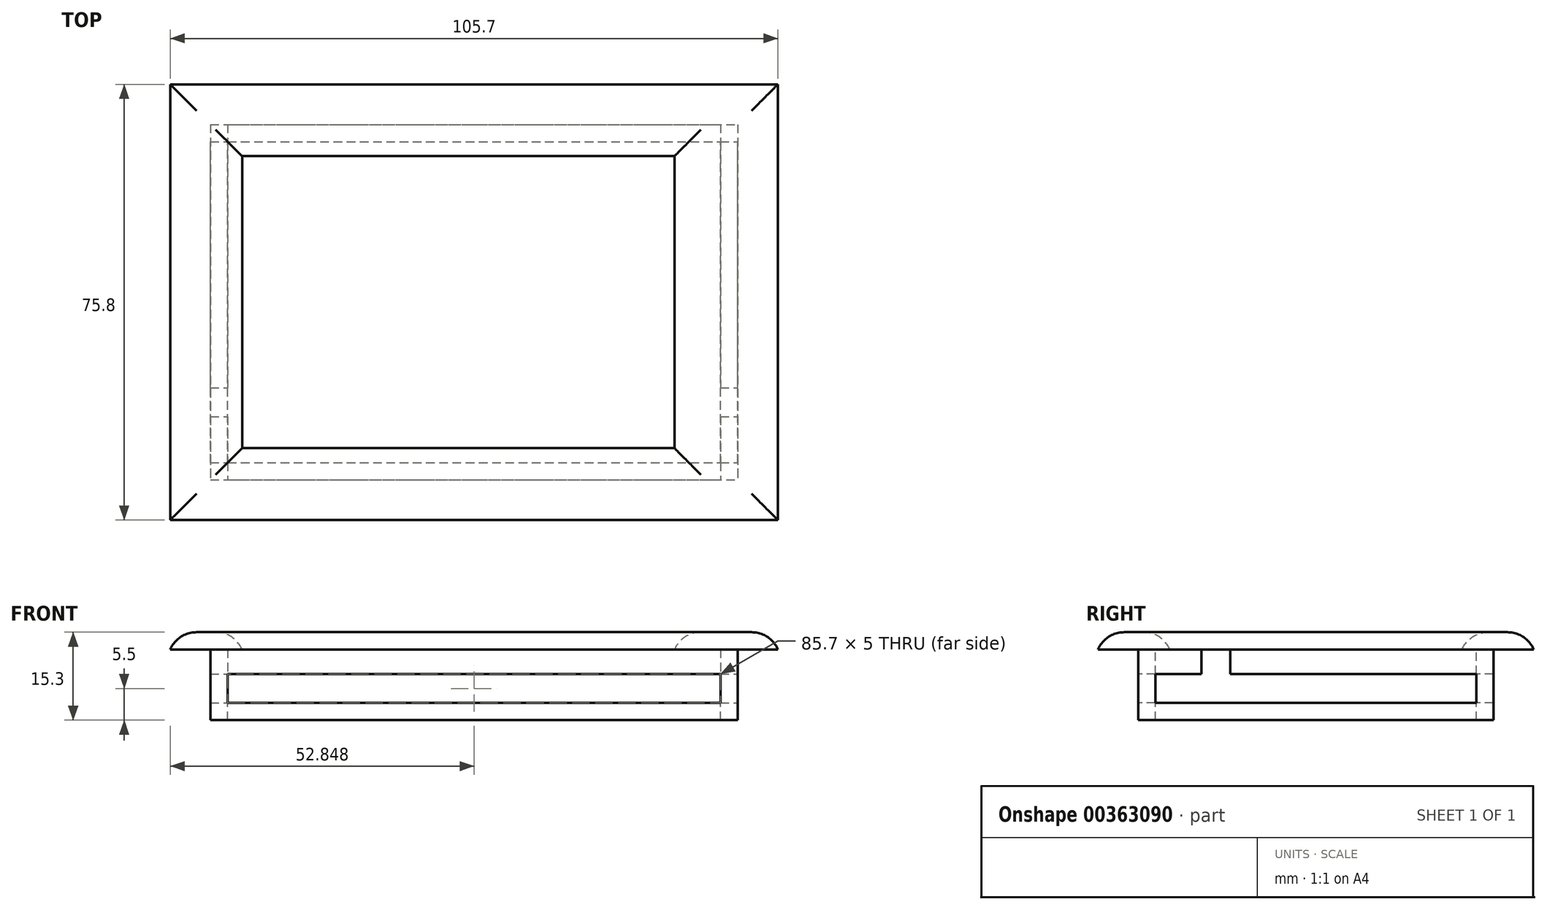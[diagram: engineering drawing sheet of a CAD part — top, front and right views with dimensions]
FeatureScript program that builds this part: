
annotation { "Feature Type Name" : "Feature", "Feature Type Description" : "" }
export const myFeature = defineFeature(function(context is Context, id is Id, definition is map)
    precondition{}
    {
        {
            assignVariable(context, id + "F0", {"name" : "tykkelse", "anyValue" : 6.3 * mm});
        }
        {
            assignVariable(context, id + "F1", {"name" : "godstykkelse", "anyValue" : 3 * mm});
        }
        {
            var Q0;
            Q0=qCreatedBy(makeId("Top.planeOp"),FACE);
            var sketch = newSketch(context, id + "F2", { "sketchPlane" : qUnion([Q0])});
            skLineSegment(sketch, "E0.bottom", {"start": v(-58.61, 40.42) * mm, "end": v(27.09, 40.42) * mm});
            skLineSegment(sketch, "E0.top", {"start": v(-58.61, -15.38) * mm, "end": v(27.09, -15.38) * mm});
            skLineSegment(sketch, "E0.left", {"start": v(-58.61, 40.42) * mm, "end": v(-58.61, -15.38) * mm});
            skLineSegment(sketch, "E0.right", {"start": v(27.09, 40.42) * mm, "end": v(27.09, -15.38) * mm});
            skLineSegment(sketch, "E1.0", {"start": v(-68.61, 50.42) * mm, "end": v(37.09, 50.42) * mm});
            skLineSegment(sketch, "E1.1", {"start": v(-68.61, 50.42) * mm, "end": v(-68.61, -25.38) * mm});
            skLineSegment(sketch, "E1.2", {"start": v(-68.61, -25.38) * mm, "end": v(37.09, -25.38) * mm});
            skLineSegment(sketch, "E1.3", {"start": v(37.09, 50.42) * mm, "end": v(37.09, -25.38) * mm});
            skLineSegment(sketch, "E2.0", {"start": v(-56.11, 37.92) * mm, "end": v(27.09, 37.92) * mm});
            skLineSegment(sketch, "E2.1", {"start": v(-56.11, 37.92) * mm, "end": v(-56.11, -12.88) * mm});
            skLineSegment(sketch, "E2.2", {"start": v(-56.11, -12.88) * mm, "end": v(27.09, -12.88) * mm});
            skLineSegment(sketch, "E3.0", {"start": v(19.09, 40.42) * mm, "end": v(19.09, -15.38) * mm});
            skSolve(sketch);
        }
        {
            var Q0;
            Q0=qCreatedBy(makeId("Top.planeOp"),FACE);
            var sketch = newSketch(context, id + "F3", { "sketchPlane" : qUnion([Q0])});
            skLineSegment(sketch, "E4.0", {"start": v(-58.61, 40.42) * mm, "end": v(27.09, 40.42) * mm});
            skPoint(sketch, "E4.1", {"position": v(-58.61, 40.42) * mm});
            skLineSegment(sketch, "E4.2", {"start": v(-58.61, 40.42) * mm, "end": v(-58.61, -15.38) * mm});
            skPoint(sketch, "E4.3", {"position": v(-58.61, -15.38) * mm});
            skLineSegment(sketch, "E4.4", {"start": v(-58.61, -15.38) * mm, "end": v(27.09, -15.38) * mm});
            skPoint(sketch, "E4.5", {"position": v(27.09, -15.38) * mm});
            skLineSegment(sketch, "E4.6", {"start": v(27.09, 40.42) * mm, "end": v(27.09, -15.38) * mm});
            skPoint(sketch, "E4.7", {"position": v(27.09, 40.42) * mm});
            skLineSegment(sketch, "E5.0", {"start": v(-61.61, 43.42) * mm, "end": v(30.09, 43.42) * mm});
            skLineSegment(sketch, "E5.1", {"start": v(-61.61, 43.42) * mm, "end": v(-61.61, -18.38) * mm});
            skLineSegment(sketch, "E5.2", {"start": v(-61.61, -18.38) * mm, "end": v(30.09, -18.38) * mm});
            skLineSegment(sketch, "E5.3", {"start": v(30.09, 43.42) * mm, "end": v(30.09, -18.38) * mm});
            skLineSegment(sketch, "E6.0", {"start": v(-64.61, 46.42) * mm, "end": v(33.09, 46.42) * mm});
            skLineSegment(sketch, "E6.1", {"start": v(-64.61, 46.42) * mm, "end": v(-64.61, -21.38) * mm});
            skLineSegment(sketch, "E6.2", {"start": v(-64.61, -21.38) * mm, "end": v(33.09, -21.38) * mm});
            skLineSegment(sketch, "E6.3", {"start": v(33.09, 46.42) * mm, "end": v(33.09, -21.38) * mm});
            skSolve(sketch);
        }
        {
            var Q0;
            Q0 = qSketchRegion(id + "F2", true);
            var Q1;
            {var subQ0=sQuery(id+"F2.wireOp",EDGE,"E0.left");Q1=makeQuery(id+"F2.imprint","IMPRINT",FACE,{"disambiguationData":[TD([[makeQuery(id+"F2.imprint","IMPRINT",EDGE,{"derivedFrom":subQ0}),1.0]])]});}
            var Q2;
            {var subQ0=sQuery(id+"F2.wireOp",EDGE,"E0.right");var subQ1=sQuery(id+"F2.wireOp",EDGE,"E0.bottom");var subQ2=makeQuery(id+"F2.imprint","INTERSECT",VERTEX,{"derivedFrom":[subQ1,subQ0]});Q2=makeQuery(id+"F2.imprint","IMPRINT",FACE,{"disambiguationData":[TD([[makeQuery(id+"F2.imprint","IMPRINT",EDGE,{"disambiguationData":[TD([[subQ2,1.0]])],"derivedFrom":subQ1}),-1.0]])]});}
            var Q3;
            {var subQ0=sQuery(id+"F2.wireOp",EDGE,"E2.0");var subQ1=sQuery(id+"F2.wireOp",EDGE,"E0.right");var subQ2=makeQuery(id+"F2.imprint","INTERSECT",VERTEX,{"derivedFrom":[subQ1,subQ0]});Q3=makeQuery(id+"F2.imprint","IMPRINT",FACE,{"disambiguationData":[TD([[makeQuery(id+"F2.imprint","IMPRINT",EDGE,{"disambiguationData":[TD([[subQ2,-1.0]])],"derivedFrom":subQ1}),-1.0]])]});}
            var Q4;
            {var subQ0=sQuery(id+"F2.wireOp",EDGE,"E0.right");var subQ1=sQuery(id+"F2.wireOp",EDGE,"E0.top");var subQ2=makeQuery(id+"F2.imprint","INTERSECT",VERTEX,{"derivedFrom":[subQ1,subQ0]});Q4=makeQuery(id+"F2.imprint","IMPRINT",FACE,{"disambiguationData":[TD([[makeQuery(id+"F2.imprint","IMPRINT",EDGE,{"disambiguationData":[TD([[subQ2,1.0]])],"derivedFrom":subQ1}),1.0]])]});}
            extrude(context, id + "F4", {"entities" : qUnion([Q0, Q1, Q2, Q3, Q4]), "depth" : getVariable(context, 'godstykkelse')});
        }
        {
            var Q0;
            Q0=makeQuery(id+"F3.imprint","IMPRINT",FACE,{"disambiguationData":[TD([[makeQuery(id+"F3.imprint","IMPRINT",EDGE,{"derivedFrom":sQuery(id+"F3.wireOp",EDGE,"E4.0")}),1.0]])]});
            extrude(context, id + "F5", {"entities" : qUnion([Q0]), "operationType" : NewBodyOperationType.ADD, "oppositeDirection" : true, "depth" : getVariable(context, 'tykkelse') + (getVariable(context, 'godstykkelse') * 2)});
        }
        {
            var Q0;
            Q0=qCreatedBy(makeId("Front.planeOp"),FACE);
            var sketch = newSketch(context, id + "F6", { "sketchPlane" : qUnion([Q0])});
            skLineSegment(sketch, "E7.0", {"start": v(-61.61, 0) * mm, "end": v(30.09, 0) * mm});
            skLineSegment(sketch, "E7.1", {"start": v(-61.61, -12.3) * mm, "end": v(-61.61, 0) * mm});
            skLineSegment(sketch, "E7.2", {"start": v(-61.61, -12.3) * mm, "end": v(30.09, -12.3) * mm});
            skLineSegment(sketch, "E7.3", {"start": v(30.09, -12.3) * mm, "end": v(30.09, 0) * mm});
            skLineSegment(sketch, "E8.0", {"start": v(-58.61, -9.3) * mm, "end": v(-58.61, 0) * mm});
            skLineSegment(sketch, "E8.1", {"start": v(-58.61, -9.3) * mm, "end": v(27.09, -9.3) * mm});
            skLineSegment(sketch, "E8.2", {"start": v(27.09, -9.3) * mm, "end": v(27.09, 0) * mm});
            skLineSegment(sketch, "E9.0", {"start": v(-61.61, -4.3) * mm, "end": v(30.09, -4.3) * mm});
            skSolve(sketch);
        }
        {
            var Q0;
            {var subQ0=sQuery(id+"F6.wireOp",EDGE,"E8.1");Q0=makeQuery(id+"F6.imprint","IMPRINT",FACE,{"disambiguationData":[TD([[makeQuery(id+"F6.imprint","IMPRINT",EDGE,{"derivedFrom":subQ0}),1.0]])]});}
            extrude(context, id + "F7", {"entities" : qUnion([Q0]), "operationType" : NewBodyOperationType.REMOVE, "endBound" : BoundingType.THROUGH_ALL, "oppositeDirection" : true, "depth" : 25 * mm, "hasSecondDirection" : true, "secondDirectionOppositeDirection" : false, "secondDirectionDepth" : 25 * mm});
        }
        {
            var Q0;
            Q0=qCreatedBy(makeId("Right.planeOp"),FACE);
            var sketch = newSketch(context, id + "F8", { "sketchPlane" : qUnion([Q0])});
            skLineSegment(sketch, "E10.0", {"start": v(43.42, 0) * mm, "end": v(-18.38, 0) * mm});
            skLineSegment(sketch, "E10.1", {"start": v(-18.38, -12.3) * mm, "end": v(-18.38, 0) * mm});
            skLineSegment(sketch, "E10.2", {"start": v(43.42, -12.3) * mm, "end": v(-18.38, -12.3) * mm});
            skLineSegment(sketch, "E10.3", {"start": v(43.42, -12.3) * mm, "end": v(43.42, 0) * mm});
            skLineSegment(sketch, "E11.0", {"start": v(-15.38, -9.3) * mm, "end": v(-15.38, 0) * mm});
            skLineSegment(sketch, "E11.1", {"start": v(40.42, -9.3) * mm, "end": v(-15.38, -9.3) * mm});
            skLineSegment(sketch, "E11.2", {"start": v(40.42, -9.3) * mm, "end": v(40.42, 0) * mm});
            skLineSegment(sketch, "E12.0", {"start": v(43.42, -4.3) * mm, "end": v(-18.38, -4.3) * mm});
            skLineSegment(sketch, "E13", {"start": v(-7.38, -3.11) * mm, "end": v(-7.38, -4.3) * mm});
            skLineSegment(sketch, "E14", {"start": v(-7.38, -4.3) * mm, "end": v(-7.38, 0) * mm});
            skLineSegment(sketch, "E15", {"start": v(-2.38, -3.11) * mm, "end": v(-2.38, -4.3) * mm});
            skLineSegment(sketch, "E16", {"start": v(-2.38, -4.3) * mm, "end": v(-2.38, 0) * mm});
            skSolve(sketch);
        }
        {
            var Q0;
            {var subQ0=sQuery(id+"F8.wireOp",EDGE,"E11.1");Q0=makeQuery(id+"F8.imprint","IMPRINT",FACE,{"disambiguationData":[TD([[makeQuery(id+"F8.imprint","IMPRINT",EDGE,{"derivedFrom":subQ0}),-1.0]])]});}
            var Q1;
            {var subQ0=sQuery(id+"F8.wireOp",EDGE,"E14");var subQ3=makeQuery(id+"F8.imprint","IMPRINT",VERTEX,{"derivedFrom":subQ0});Q1=makeQuery(id+"F8.imprint","IMPRINT",FACE,{"disambiguationData":[TD([[makeQuery(id+"F8.imprint","IMPRINT",EDGE,{"disambiguationData":[TD([[subQ3,1.0]])],"derivedFrom":subQ0}),-1.0]])]});}
            extrude(context, id + "F9", {"entities" : qUnion([Q0, Q1]), "operationType" : NewBodyOperationType.REMOVE, "endBound" : BoundingType.THROUGH_ALL, "oppositeDirection" : true, "depth" : 25 * mm, "hasSecondDirection" : true, "secondDirectionBound" : SecondDirectionBoundingType.THROUGH_ALL, "secondDirectionOppositeDirection" : false, "secondDirectionDepth" : 25 * mm});
        }
        {
            var Q0;
            Q0=makeQuery(id+"F4.opExtrude","CAP_FACE",FACE,{"disambiguationData":[OSD([sQuery(id+"F2.wireOp",EDGE,"E1.0"),sQuery(id+"F2.wireOp",EDGE,"E1.1"),sQuery(id+"F2.wireOp",EDGE,"E1.2"),sQuery(id+"F2.wireOp",EDGE,"E1.3"),sQuery(id+"F2.wireOp",EDGE,"E2.0"),sQuery(id+"F2.wireOp",EDGE,"E2.1"),sQuery(id+"F2.wireOp",EDGE,"E2.2"),sQuery(id+"F2.wireOp",EDGE,"E3.0")])],"isStart":false});
            fillet(context, id + "F10", {"entities" : qUnion([Q0]), "radius" : 5 * mm, "tangentPropagation" : true, "allowEdgeOverflow" : false});
        }
    });
